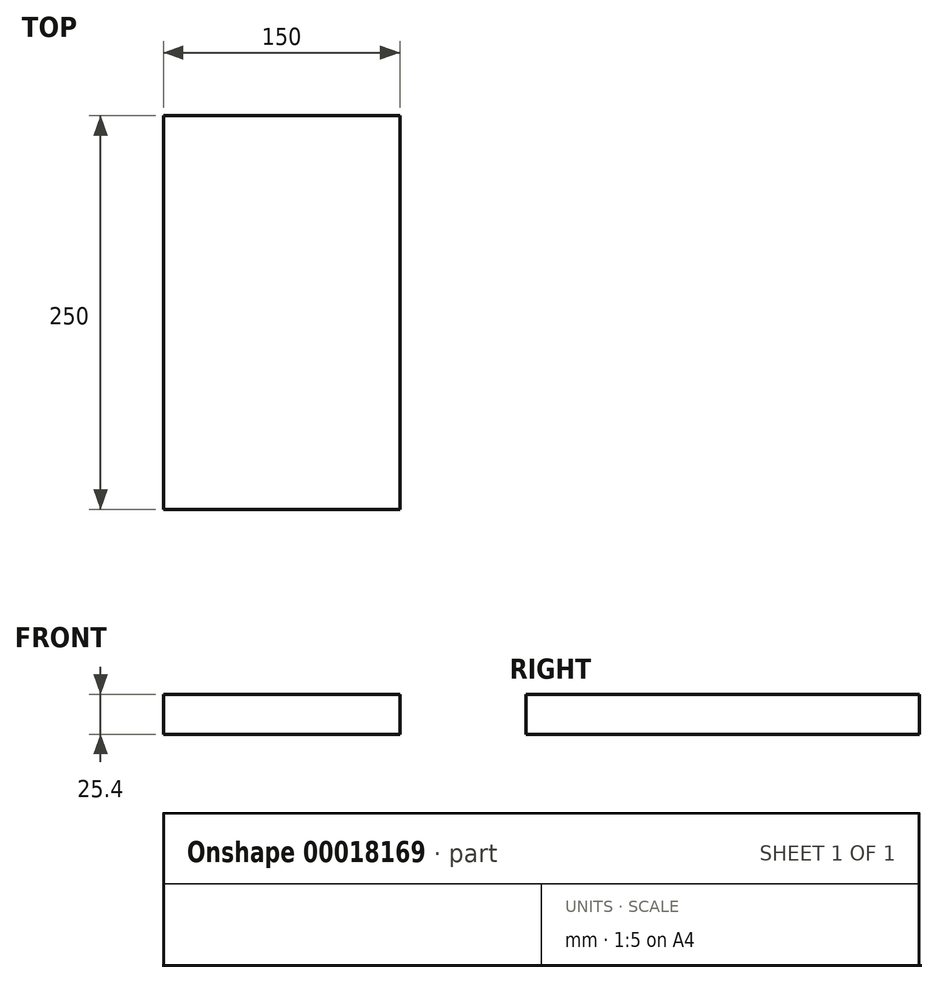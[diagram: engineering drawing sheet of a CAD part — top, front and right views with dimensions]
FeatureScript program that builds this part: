
annotation { "Feature Type Name" : "Feature", "Feature Type Description" : "" }
export const myFeature = defineFeature(function(context is Context, id is Id, definition is map)
    precondition{}
    {
        {
            var Q0;
            Q0=qCreatedBy(makeId("Top.planeOp"),FACE);
            var sketch = newSketch(context, id + "F0", { "sketchPlane" : qUnion([Q0])});
            skLineSegment(sketch, "E0.rect.bottom", {"start": v(75, -125) * mm, "end": v(-75, -125) * mm});
            skLineSegment(sketch, "E0.rect.top", {"start": v(75, 125) * mm, "end": v(-75, 125) * mm});
            skLineSegment(sketch, "E0.rect.left", {"start": v(75, -125) * mm, "end": v(75, 125) * mm});
            skLineSegment(sketch, "E0.rect.right", {"start": v(-75, -125) * mm, "end": v(-75, 125) * mm});
            skPoint(sketch, "E0.rect.middle", {"position": v(0, 0) * mm});
            skSolve(sketch);
        }
        {
            var Q0;
            Q0 = qConstructionFilter(qBodyType(qCreatedBy(id + "F0" ,EDGE), BodyType.WIRE), ConstructionObject.NO);
            extrude(context, id + "F1", {"bodyType" : ToolBodyType.SURFACE, "surfaceEntities" : qUnion([Q0]), "depth" : 25.4 * mm});
        }
    });
